# Revit family: xLIFE-PRO-RECWP-xx_Non-Hosted_R16
name_source: partatom
category: Lighting Fixtures
revit_build: Autodesk Revit 2016 (Build: 20151007_0715(x64)
units: mm (PartAtom-declared; Revit-internal decimal feet)

## family parameters
Always vertical = Yes
Cut with Voids When Loaded = No
Light Source = Yes
OmniClass Number = 23.80.70.00
OmniClass Title = Lighting
Part Type = Normal
Room Calculation Point = No
Round Connector Dimension = Use Diameter
Shared = No
Work Plane-Based = No

## types (10) — shared parameters
AS2293 Classification = C0=D40 C90=D40
Battery = 3.2V 6400mAh
Battery Type = Lithium Iron Phosphate
Ceiling Hole Cut-Out = 106mm
Charging Method = Intelligent current limited constant voltage
Color Filter = 16777215
Construction (Head) = Die Cast Aluminium Body, 316 Stainless Steel Screws
Diffuser = Clear Toughen Glass
Dimensions L x W x H (Head) = 120mm head diameter
Dimming Lamp Color Temperature Shift = <None>
Emergency Lumen Output = 336.5 lm
Emit Shape Visible in Rendering = No
Emit from Rectangle Length = 1219 mm
Emit from Rectangle Width = 610 mm
IK Rating = IK10
IP Rating = IP65 (Head only)
Lamp = Dual LED (Lifetime warranty on the lamp head and loom assembly)
Manufacturer = Clevertronics
Minimum Ceiling Depth = 120mm
Mounting = Recessed Ceiling
Operating Mode = Non-maintained
Operating Temperature = 0˚C to 40˚C
Operating Voltage = 240V AC 50Hz
Photometric Web File = 200409PH CLIFE-PRO-HV-RECWP-WHT AS2293.3 Photometry.ies
Power Consumption (Standby) = 0.4W
Replacement Emergency Battery = 1550230 BATT:LP 3.2V 6400mAh.200mm lead.Brkt.
Tilt Angle = 90.00°

## per-type parameters (varying)
| type | Dimensions L x W x H (Control Pack) | MIC Number | Power Consumption (Max) | Product Description | Replacement Emergency Driver | Replacement Emergency Lamp | Testing Node | Testing System | Weight |
| CLIFE-PRO-ZW-RECWP-WHT | 232mm x 40mm x 40mm | AUT02120020001 | 4.7W | LP Premium LifeLight PRO, high performance, IP65 recessed Emergency Light with remote
gear | CLIFE-PRO-CKIT Lifelight Pro, LP Lithium, Parts Kit | 1100835 Lifelight Pro Head Assembly, Round,Black | 8001450 PCA:Powerline Node ZW, #CT10310-A6 | Zoneworks Computerised Testing |  |
| CLIFE-PRO-ZW-RECWP-BLK | 232mm x 40mm x 40mm | AUT02120070001 | 4.7W | LP Premium LifeLight PRO, high performance, IP65 recessed Emergency Light with remote
gear | CLIFE-PRO-CKIT Lifelight Pro, LP Lithium, Parts Kit | 1100835 Lifelight Pro Head Assembly, Round,Black | 8001450 PCA:Powerline Node ZW, #CT10310-A6 | Zoneworks Computerised Testing |  |
| CLIFE-PRO-DALI-RECWP-WHT | 232mm x 40mm x 40mm | AUT02220010102 | 4.7W | LP Premium LifeLight PRO, high performance, IP65 recessed Emergency Light with
remote gear | CLIFE-PRO-CKIT Lifelight Pro, LP Lithium, Parts Kit | 1100835 Lifelight Pro Head Assembly, Round,Black | 8003060 PCA: DALI Node #CT10629-Ax | DALI Registered | 1.75kg |
| CLIFE-PRO-RECWP-WHT | 232mm x 40mm x 40mm | AUT02320060001 | 2.7 Watts | LP Premium LifeLight PRO, high performance, IP65 recessed Emergency Light with remote gear, Enabled with Clevertest Plus | CLIFE-PRO-CKIT  Lifelight Pro, Control Only, LP Lithium | 1100843 Lifelight Pro Head Assembly, Round, Blk, Gen 2 |  | Clevertest Plus Enabled (Not activated by default) | 1.75kg |
| CLIFE-PRO-RECWP-BLK | 232mm x 40mm x 40mm | AUT02320110001 | 4.7 Watts | LP Premium LifeLight PRO, high performance, IP65 recessed Emergency Light with remote
gear, Enabled with Clevertest Plus | CLIFE-PRO-PKIT Lifelight Pro, LP Lithium, Parts Kit | 1100835 Lifelight Pro Head Assembly, Round,Black |  | Clevertest Plus Enabled (Not activated by default) | 1.75kg |
| CLIFE-PRO-HV-RECWP-TP-WHT | 232mm x 40mm x 40mm | AUT02810030001 | 4.7 Watts | LP Premium LifeLight PRO, High Performance, IP65 recessed Emergency Light with
Remote Gear and Tamper Proof Screws | CLIFE-PRO-CKIT  Lifelight Pro, Control Only, LP Lithium | 1100843 Lifelight Pro Head Assembly, Round, Blk, Gen 2 | 8003190 PCA: RF Node CT10678-Ax internal antenna | Zoneworks XTHIVE (RF) | 1.75kg |
| CLIFE-PRO-HV-RECWP-WHT | 232mm x 40mm x 40mm | AUT02820040001 | 4.7 Watts | LP Premium LifeLight PRO, high performance, IP65 recessed Emergency Light with
remote gear | CLIFE-PRO-CKIT-HV Lifelight Pro, Control Only, LP, HV | 1100843 Lifelight Pro Head Assembly, Round, Blk, Gen 2 | 8003191 PCA: RF Node CT10678-A9 Int Antenna LLPro | Zoneworks XT HIVE (RF) | 1.75kg |
| CLIFE-PRO-RECWP-IPREM-WHT | 360mm x 160mm x 100mm |  | 4.7 Watts | LP Premium LifeLight PRO, high performance, IP65 recessed Emergency Light with IP66/67 remote control gear, White, Enabled with Clevertest Plus | CLIFE-PRO-CKIT-NP LifelightPro,Control Only,Batten,LP, NP | 1100843 Lifelight Pro Head Assembly, Round, Blk, Gen 2 |  | Clevertest Plus Enabled (Not activated by default) | 1.75kg |
| CLIFE-PRO-RECWP-TP-WHT | 360mm x 160mm x 100mm |  | 4.7 Watts | LP Premium LifeLight PRO, high performance, IP65 recessed Emergency with tamper proof screws, White, Enabled with Clevertest Plus | CLIFE-PRO-CKIT Lifelight Pro, Control Only, LP Lithium | 1100843 Lifelight Pro Head Assembly, Round, Blk, Gen 2 |  | Clevertest Plus Enabled (Not activated by default) | 1.75kg |
| CLIFE-PRO-ZW-RECWP-TP-WHT | 360mm x 160mm x 100mm |  | 4.7 Watts | LP Premium LifeLight PRO, high performance, IP65 recessed Emergency Light with remote
gear and tamperproof screws | CLIFE-PRO-CKIT Lifelight Pro, Control Only, LP Lithium | 1100835 Lifelight Pro Head Assembly, Round,Black | 8001450 PCA:Powerline Node ZW, #CT10310-A6 | Zoneworks Computerised Testing | 1.75kg |

note: column(s) folded — value = type name in every type: Model

## geometry (parser evidence)
native form markers: Sweep x2
no freeform markers — native parametric forms only
